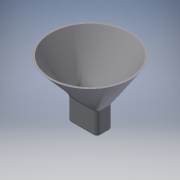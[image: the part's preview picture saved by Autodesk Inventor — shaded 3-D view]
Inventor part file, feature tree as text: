
AUTODESK INVENTOR PART (.ipt)
format: ipt  version: 2016 (Build 200138000, 138)  size: 1,247,744 bytes
history: native  units: mm
features: fillet x14, sketch x3, loft x2, other x2, extrude x1, plane x1
ambient origin geometry x8: Origin, YZ Plane, XZ Plane, XY Plane, X Axis, Y Axis, Z Axis, Center Point
bodies: Solid1 (feature_tree)
feature tree (23):
  extrude  "Extrusion1"  Depth=21.0mm
  plane  "Work Plane1"
  loft  "Loft2"
  loft  "Loft3"
  fillet  "Fillet10"  [1 undecoded]
  fillet  "Fillet11"  [1 undecoded]
  fillet  "Fillet12"  Radius=104.0mm
  fillet  "Fillet13"  [1 undecoded]
  fillet  "Fillet17"  [1 undecoded]
  fillet  "Fillet1"  Radius=10.0mm
  fillet  "Fillet2"  Radius=5.0mm
  fillet  "Fillet4"  Radius=12.0mm
  fillet  "Fillet15"  Radius=3.69mm
  fillet  "Fillet5"  Radius=11.2mm
  fillet  "Fillet6"  Radius=23.4mm
  fillet  "Fillet7"  Radius=2.0mm
  fillet  "Fillet8"  Radius=1.0mm
  fillet  "Fillet3"  Radius=10.0mm
  sketch  "Sketch1"  dims[d0=40.0mm d1=21.0mm]
  sketch  "Sketch2"  dims[d2=1.5mm d3=30.0mm d4=0.0mm]
  other  "Edges6"
  sketch  "Sketch3"  dims[d5=50.0mm d6=110.0mm d26=0.0mm d27=90.0deg d28=0.0mm d29=90.0deg d30=104.0mm d31=0.0mm d32=90.0deg d33=0.0mm d34=90.0deg d35=10.0mm d36=5.0mm d37=12.0mm d38=3.69mm d39=11.2mm d40=23.4mm d41=2.0mm d42=1.0mm d44=10.0mm d45=20.0mm d46=5.0mm d47=5.0mm d49=2.0mm d51=2.0mm]
  other  "Edges7"
note: 4 required parameter values undecoded (feature->parameter linkage not recoverable at this tier; creation-order binding heuristic only, values carry confidence <= 0.55)
